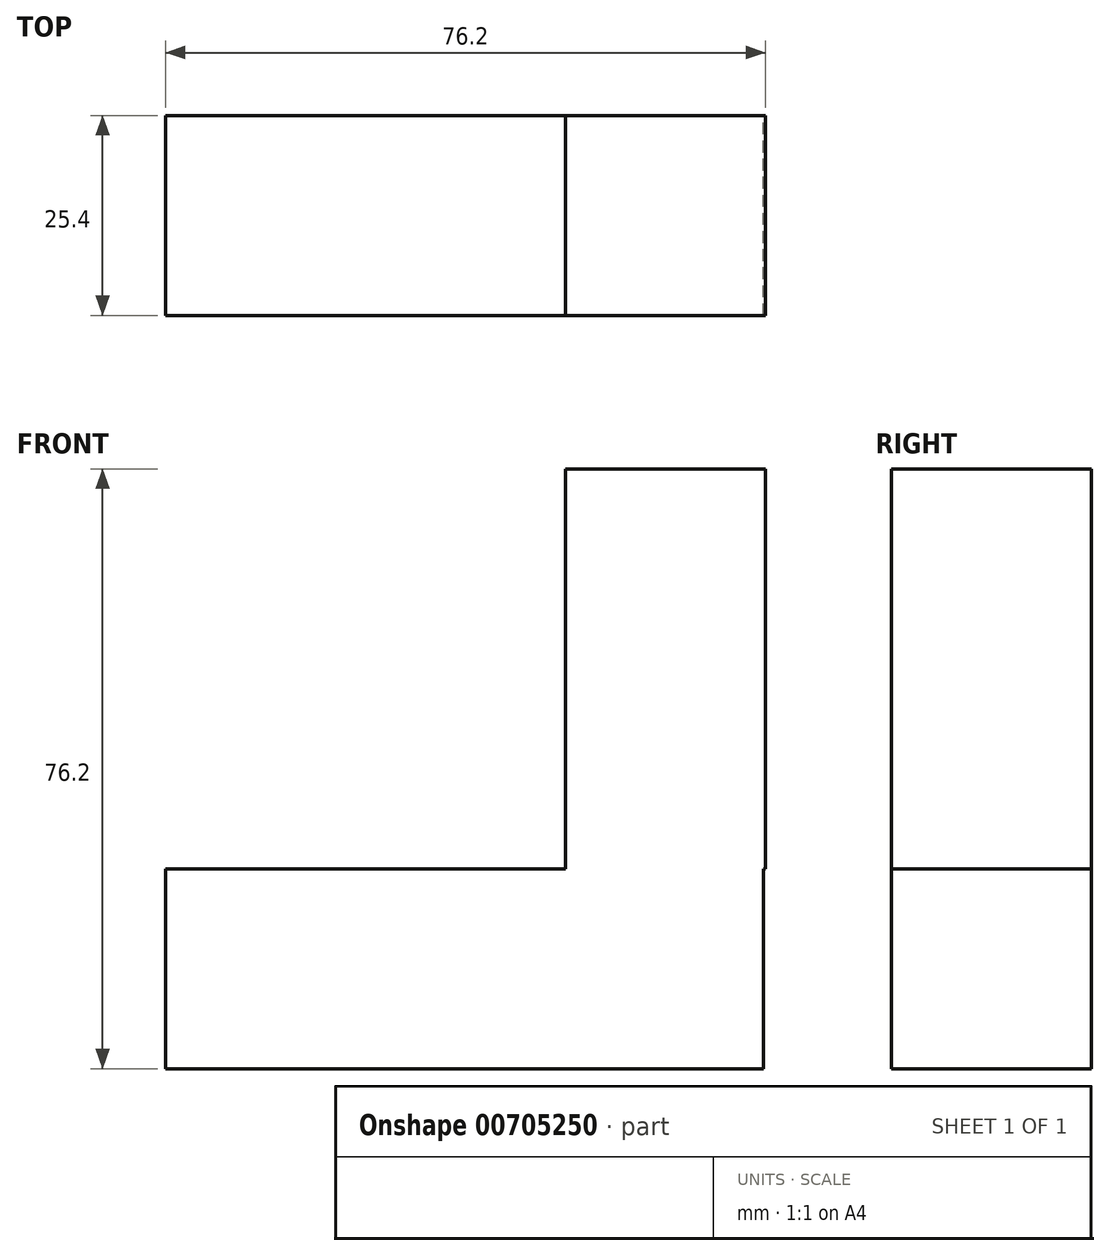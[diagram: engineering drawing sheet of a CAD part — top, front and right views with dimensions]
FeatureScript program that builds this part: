
annotation { "Feature Type Name" : "Feature", "Feature Type Description" : "" }
export const myFeature = defineFeature(function(context is Context, id is Id, definition is map)
    precondition{}
    {
        {
            var Q0;
            Q0=qCreatedBy(makeId("Front.planeOp"),FACE);
            var sketch = newSketch(context, id + "F0", { "sketchPlane" : qUnion([Q0])});
            skLineSegment(sketch, "E0.bottom", {"start": v(0, 0) * mm, "end": v(25.14, 0) * mm});
            skLineSegment(sketch, "E0.top", {"start": v(0, -25.4) * mm, "end": v(25.14, -25.4) * mm});
            skLineSegment(sketch, "E0.left", {"start": v(0, 0) * mm, "end": v(0, -25.4) * mm});
            skLineSegment(sketch, "E0.right", {"start": v(25.14, 0) * mm, "end": v(25.14, -25.4) * mm});
            skLineSegment(sketch, "E1.bottom", {"start": v(0, -25.4) * mm, "end": v(-25.4, -25.4) * mm});
            skLineSegment(sketch, "E1.top", {"start": v(0, 0) * mm, "end": v(-25.4, 0) * mm});
            skLineSegment(sketch, "E1.left", {"start": v(0, -25.4) * mm, "end": v(0, 0) * mm});
            skLineSegment(sketch, "E1.right", {"start": v(-25.4, -25.4) * mm, "end": v(-25.4, 0) * mm});
            skLineSegment(sketch, "E2.bottom", {"start": v(-25.4, 0) * mm, "end": v(-50.8, 0) * mm});
            skLineSegment(sketch, "E2.top", {"start": v(-25.4, -25.4) * mm, "end": v(-50.8, -25.4) * mm});
            skLineSegment(sketch, "E2.left", {"start": v(-25.4, 0) * mm, "end": v(-25.4, -25.4) * mm});
            skLineSegment(sketch, "E2.right", {"start": v(-50.8, 0) * mm, "end": v(-50.8, -25.4) * mm});
            skLineSegment(sketch, "E3.bottom", {"start": v(0, 0) * mm, "end": v(25.4, 0) * mm});
            skLineSegment(sketch, "E3.top", {"start": v(0, 25.4) * mm, "end": v(25.4, 25.4) * mm});
            skLineSegment(sketch, "E3.left", {"start": v(0, 0) * mm, "end": v(0, 25.4) * mm});
            skLineSegment(sketch, "E3.right", {"start": v(25.4, 0) * mm, "end": v(25.4, 25.4) * mm});
            skLineSegment(sketch, "E4.bottom", {"start": v(25.4, 25.4) * mm, "end": v(0, 25.4) * mm});
            skLineSegment(sketch, "E4.top", {"start": v(25.4, 50.8) * mm, "end": v(0, 50.8) * mm});
            skLineSegment(sketch, "E4.left", {"start": v(25.4, 25.4) * mm, "end": v(25.4, 50.8) * mm});
            skLineSegment(sketch, "E4.right", {"start": v(0, 25.4) * mm, "end": v(0, 50.8) * mm});
            skSolve(sketch);
        }
        {
            var Q0;
            Q0 = qSketchRegion(id + "F0", true);
            extrude(context, id + "F1", {"entities" : qUnion([Q0]), "depth" : 25.4 * mm, "offsetDistance" : 25.4 * mm});
        }
    });
